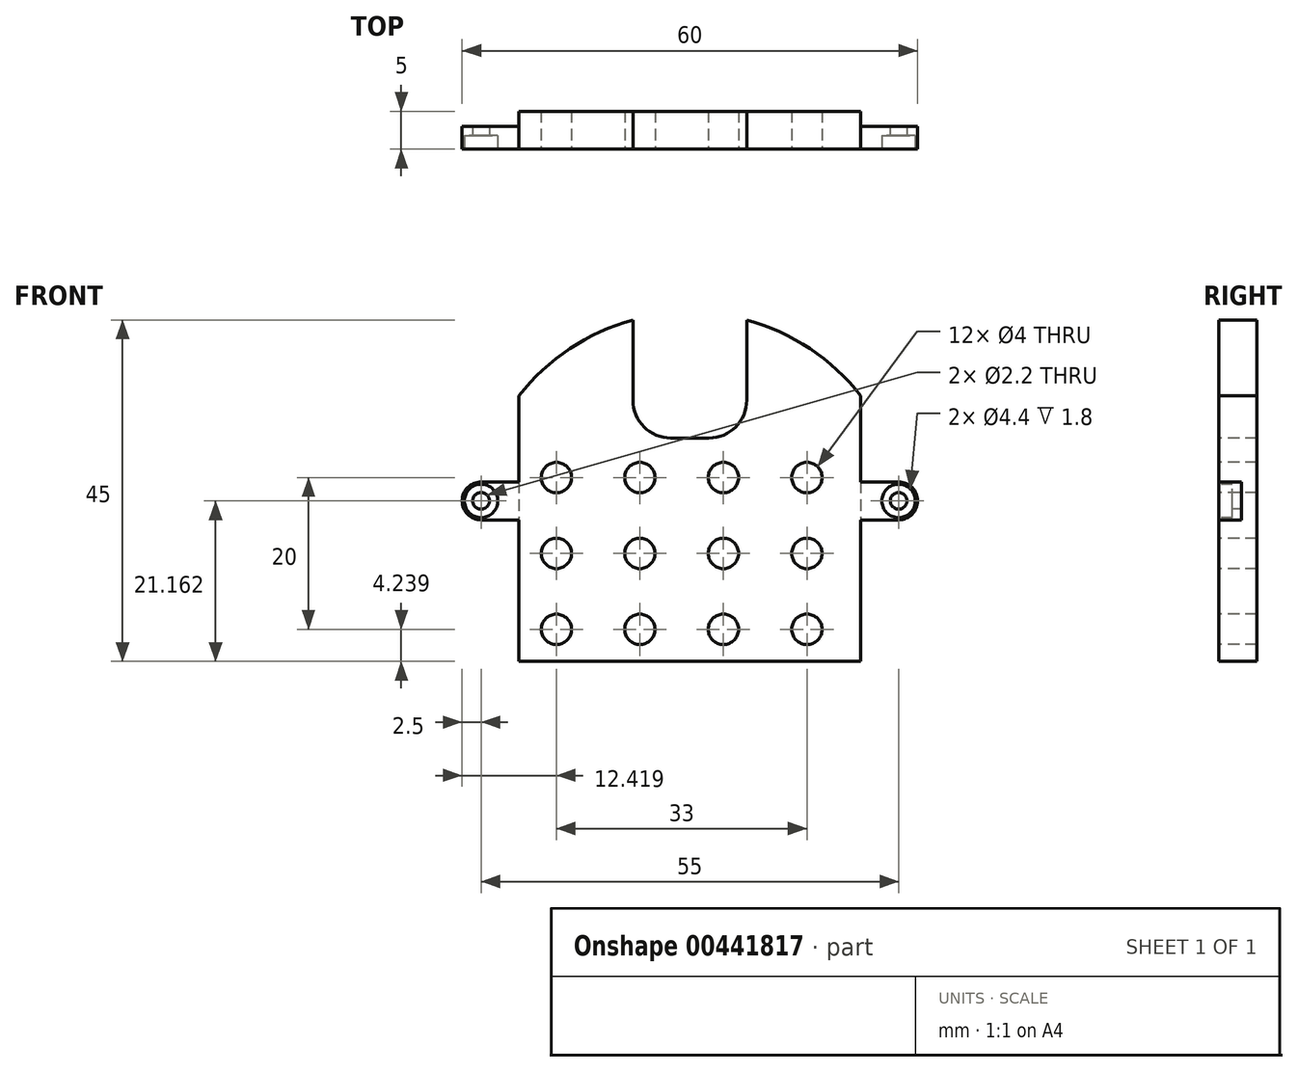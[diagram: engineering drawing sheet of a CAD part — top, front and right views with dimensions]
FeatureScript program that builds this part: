
annotation { "Feature Type Name" : "Feature", "Feature Type Description" : "" }
export const myFeature = defineFeature(function(context is Context, id is Id, definition is map)
    precondition{}
    {
        {
            var Q0;
            Q0=qCreatedBy(makeId("Front.planeOp"),FACE);
            var sketch = newSketch(context, id + "F0", { "sketchPlane" : qUnion([Q0])});
            skLineSegment(sketch, "E0.top", {"start": v(22.5, -17.5) * mm, "end": v(-22.5, -17.5) * mm});
            skLineSegment(sketch, "E0.left", {"start": v(22.5, 17.5) * mm, "end": v(22.5, -17.5) * mm});
            skLineSegment(sketch, "E0.right", {"start": v(-22.5, 17.5) * mm, "end": v(-22.5, -17.5) * mm});
            skPoint(sketch, "E0.middle", {"position": v(0, 0) * mm});
            skArc(sketch, "E1", {"start": v(22.5, 17.5) * mm, "mid": v(0, 28.5) * mm, "end": v(-22.5, 17.5) * mm});
            skSolve(sketch);
        }
        {
            var Q0;
            Q0 = qSketchRegion(id + "F0", true);
            extrude(context, id + "F1", {"entities" : qUnion([Q0]), "depth" : 5 * mm});
        }
        {
            var Q0;
            Q0=makeQuery(id+"F1.opExtrude","CAP_FACE",FACE,{"disambiguationData":[OSD([sQuery(id+"F0.wireOp",EDGE,"E0.top"),sQuery(id+"F0.wireOp",EDGE,"E0.left"),sQuery(id+"F0.wireOp",EDGE,"E0.right"),sQuery(id+"F0.wireOp",EDGE,"E1")])],"isStart":false});
            var sketch = newSketch(context, id + "F2", { "sketchPlane" : qUnion([Q0])});
            skLineSegment(sketch, "E2.bottom", {"start": v(-7.5, 45.07) * mm, "end": v(7.5, 45.07) * mm});
            skLineSegment(sketch, "E2.top", {"start": v(-7.5, 11.94) * mm, "end": v(7.5, 11.94) * mm});
            skLineSegment(sketch, "E2.left", {"start": v(-7.5, 45.07) * mm, "end": v(-7.5, 11.94) * mm});
            skLineSegment(sketch, "E2.right", {"start": v(7.5, 45.07) * mm, "end": v(7.5, 11.94) * mm});
            skPoint(sketch, "E2.middle", {"position": v(0, 28.5) * mm});
            skSolve(sketch);
        }
        {
            var Q0;
            Q0 = qSketchRegion(id + "F2", true);
            extrude(context, id + "F3", {"entities" : qUnion([Q0]), "operationType" : NewBodyOperationType.REMOVE, "oppositeDirection" : true, "depth" : 25 * mm});
        }
        {
            var Q0;
            Q0=makeQuery(id+"F3.boolean.opBoolean","COPY",EDGE,{"derivedFrom":makeQuery(id+"F3.opExtrude","SWEPT_EDGE",EDGE,{"disambiguationData":[OSD([sQuery(id+"F2.wireOp",EDGE,"E2.top"),sQuery(id+"F2.wireOp",EDGE,"E2.left")])]})});
            var Q1;
            Q1=makeQuery(id+"F3.boolean.opBoolean","COPY",EDGE,{"derivedFrom":makeQuery(id+"F3.opExtrude","SWEPT_EDGE",EDGE,{"disambiguationData":[OSD([sQuery(id+"F2.wireOp",EDGE,"E2.top"),sQuery(id+"F2.wireOp",EDGE,"E2.right")])]})});
            fillet(context, id + "F4", {"entities" : qUnion([Q0, Q1]), "radius" : 5 * mm, "tangentPropagation" : true, "allowEdgeOverflow" : false});
        }
        {
            var Q0;
            Q0=makeQuery(id+"F1.opExtrude","CAP_FACE",FACE,{"disambiguationData":[OSD([sQuery(id+"F0.wireOp",EDGE,"E0.top"),sQuery(id+"F0.wireOp",EDGE,"E0.left"),sQuery(id+"F0.wireOp",EDGE,"E0.right"),sQuery(id+"F0.wireOp",EDGE,"E1")])],"isStart":false});
            var sketch = newSketch(context, id + "F5", { "sketchPlane" : qUnion([Q0])});
            skLineSegment(sketch, "E3", {"start": v(-22.5, 6.16) * mm, "end": v(-27.5, 6.16) * mm});
            skLineSegment(sketch, "E4", {"start": v(-27.5, 1.16) * mm, "end": v(-22.5, 1.16) * mm});
            skLineSegment(sketch, "E5", {"start": v(-22.5, 1.16) * mm, "end": v(-22.5, 6.16) * mm});
            skLineSegment(sketch, "E6", {"start": v(22.5, 0) * mm, "end": v(-22.5, 0) * mm, "construction": true});
            skArc(sketch, "E7", {"start": v(-27.5, 6.16) * mm, "mid": v(-30, 3.66) * mm, "end": v(-27.5, 1.16) * mm});
            skLineSegment(sketch, "E8", {"start": v(0, -17.5) * mm, "end": v(0, -14.5) * mm, "construction": true});
            skPoint(sketch, "E8.endSnap0", {"position": v(0, -17.5) * mm});
            skLineSegment(sketch, "E9.MirrorCS", {"start": v(27.5, 1.16) * mm, "end": v(22.5, 1.16) * mm});
            skArc(sketch, "E10.MirrorCS", {"start": v(27.5, 6.16) * mm, "mid": v(30, 3.66) * mm, "end": v(27.5, 1.16) * mm});
            skLineSegment(sketch, "E11.MirrorCS", {"start": v(22.5, 1.16) * mm, "end": v(22.5, 6.16) * mm});
            skLineSegment(sketch, "E12.MirrorCS", {"start": v(22.5, 6.16) * mm, "end": v(27.5, 6.16) * mm});
            skSolve(sketch);
        }
        {
            var Q0;
            Q0 = qSketchRegion(id + "F5", true);
            extrude(context, id + "F6", {"entities" : qUnion([Q0]), "operationType" : NewBodyOperationType.ADD, "oppositeDirection" : true, "depth" : 3 * mm});
        }
        {
            var Q0;
            Q0=sQuery(id+"F5.wireOp",VERTEX,"E7.center");
            var Q1;
            Q1=sQuery(id+"F5.wireOp",VERTEX,"E10.MirrorCS.center");
            var Q2;
            Q2=makeQuery(id+"F1.opExtrude","SWEPT_BODY",BODY,{"disambiguationData":[OSD([sQuery(id+"F0.wireOp",EDGE,"E0.top"),sQuery(id+"F0.wireOp",EDGE,"E0.left"),sQuery(id+"F0.wireOp",EDGE,"E0.right"),sQuery(id+"F0.wireOp",EDGE,"E1")])]});
            hole(context, id + "F7", {"style" : HoleStyle.C_BORE, "endStyle" : HoleEndStyle.BLIND, "holeDiameter" : 2.2 * mm, "cBoreDiameter" : 4.4 * mm, "cBoreDepth" : 1.8 * mm, "holeDepth" : 40 * mm, "isTappedThrough" : true, "tappedDepth" : 12 * mm, "tapClearance" : 3, "startFromSketch" : true, "locations" : qUnion([Q0, Q1]), "scope" : qUnion([Q2])});
        }
        {
            var Q0;
            {var subQ12=sQuery(id+"F5.wireOp",EDGE,"E5");Q0=makeQuery(id+"F5.imprint","IMPRINT",FACE,{"disambiguationData":[TD([[makeQuery(id+"F5.imprint","IMPRINT",EDGE,{"derivedFrom":subQ12}),1.0]])]});}
            var sketch = newSketch(context, id + "F8", { "sketchPlane" : qUnion([Q0])});
            skCircle(sketch, "E13", {"center": v(-17.58, -13.26) * mm, "radius": 2 * mm});
            skCircle(sketch, "E14.0.1.0", {"center": v(-17.58, -3.26) * mm, "radius": 2 * mm});
            skCircle(sketch, "E14.0.2.0", {"center": v(-17.58, 6.74) * mm, "radius": 2 * mm});
            skCircle(sketch, "E14.1.0.0", {"center": v(-6.58, -13.26) * mm, "radius": 2 * mm});
            skCircle(sketch, "E14.1.1.0", {"center": v(-6.58, -3.26) * mm, "radius": 2 * mm});
            skCircle(sketch, "E14.1.2.0", {"center": v(-6.58, 6.74) * mm, "radius": 2 * mm});
            skCircle(sketch, "E14.2.0.0", {"center": v(4.42, -13.26) * mm, "radius": 2 * mm});
            skCircle(sketch, "E14.2.1.0", {"center": v(4.42, -3.26) * mm, "radius": 2 * mm});
            skCircle(sketch, "E14.2.2.0", {"center": v(4.42, 6.74) * mm, "radius": 2 * mm});
            skCircle(sketch, "E14.3.0.0", {"center": v(15.42, -13.26) * mm, "radius": 2 * mm});
            skCircle(sketch, "E14.3.1.0", {"center": v(15.42, -3.26) * mm, "radius": 2 * mm});
            skCircle(sketch, "E14.3.2.0", {"center": v(15.42, 6.74) * mm, "radius": 2 * mm});
            skLineSegment(sketch, "E14.direction1", {"start": v(-17.58, -13.26) * mm, "end": v(-6.58, -13.26) * mm, "construction": true});
            skLineSegment(sketch, "E14.direction2", {"start": v(-17.58, -13.26) * mm, "end": v(-17.58, -3.26) * mm, "construction": true});
            skSolve(sketch);
        }
        {
            var Q0;
            Q0 = qSketchRegion(id + "F8", true);
            extrude(context, id + "F9", {"entities" : qUnion([Q0]), "operationType" : NewBodyOperationType.REMOVE, "oppositeDirection" : true, "depth" : 25 * mm});
        }
    });
